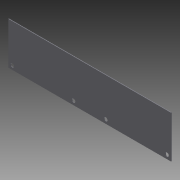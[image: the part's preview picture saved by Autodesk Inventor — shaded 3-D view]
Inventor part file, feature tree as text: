
AUTODESK INVENTOR PART (.ipt)
format: ipt  version: 2012 (Build 160160000, 160)  size: 90,112 bytes
history: native  units: in
note: dims shown in document units (in); Inventor stores cm internally (conversion verified against a paired STEP export)
features: reference x4, sketch x3, hole x2, extrude x1
ambient origin geometry x8: Origin, YZ Plane, XZ Plane, XY Plane, X Axis, Y Axis, Z Axis, Center Point
bodies: Solid1 (feature_tree)
feature tree (10):
  extrude  "Extrusion1"  Depth=2.0in
  hole  "Hole1"  [1 undecoded]
  hole  "Hole2"  [1 undecoded]
  sketch  "Sketch1"  dims[d0=7.7in d1=2.0in]
  sketch  "Sketch2"  dims[d2=0.03in d3=0.0in]
  reference  "Reference1"
  reference  "Reference2"
  reference  "Reference3"
  reference  "Reference4"
  sketch  "Sketch3"  dims[d4=0.17in d5=0.75in d6=0.332in d7=0.25in d8=0.5635in d9=1.0in d10=0.8108in d11=1.0in d12=0.6in d13=0.6in d14=1.0in d15=0.17in d16=0.75in d17=0.332in d18=0.25in d19=0.5635in d20=1.0in d21=0.8108in]
note: 2 required parameter values undecoded (feature->parameter linkage not recoverable at this tier; creation-order binding heuristic only, values carry confidence <= 0.55)
